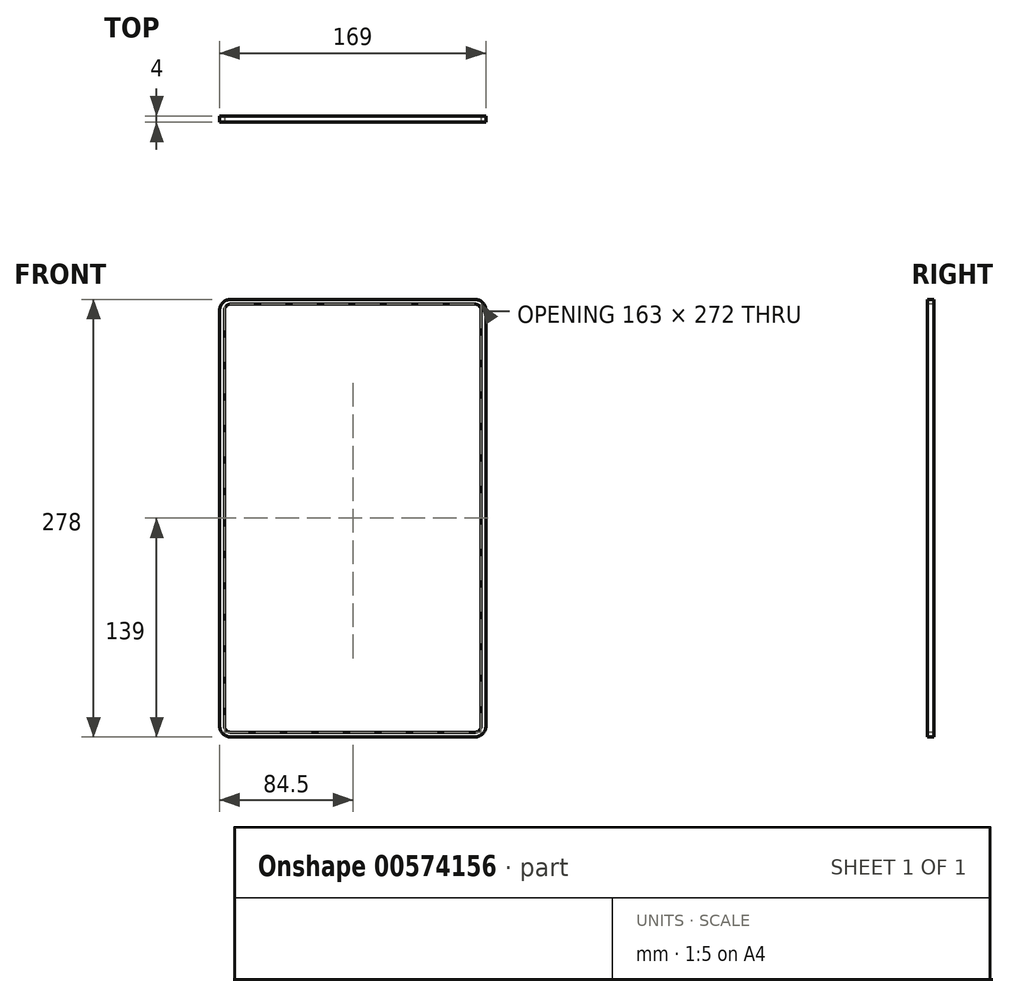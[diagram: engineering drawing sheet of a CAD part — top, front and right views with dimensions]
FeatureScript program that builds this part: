
annotation { "Feature Type Name" : "Feature", "Feature Type Description" : "" }
export const myFeature = defineFeature(function(context is Context, id is Id, definition is map)
    precondition{}
    {
        {
            var Q0;
            Q0=qCreatedBy(makeId("Front.planeOp"),FACE);
            var sketch = newSketch(context, id + "F0", { "sketchPlane" : qUnion([Q0])});
            skLineSegment(sketch, "E0.bottom", {"start": v(-77.5, 139) * mm, "end": v(77.5, 139) * mm});
            skLineSegment(sketch, "E0.top", {"start": v(-77.5, -139) * mm, "end": v(77.5, -139) * mm});
            skLineSegment(sketch, "E0.left", {"start": v(-84.5, 132) * mm, "end": v(-84.5, -132) * mm});
            skLineSegment(sketch, "E0.right", {"start": v(84.5, 132) * mm, "end": v(84.5, -132) * mm});
            skPoint(sketch, "E1.visualSharp", {"position": v(-84.5, 139) * mm});
            skArc(sketch, "E1.filletArc", {"start": v(-77.5, 139) * mm, "mid": v(-82.45, 136.95) * mm, "end": v(-84.5, 132) * mm});
            skPoint(sketch, "E2.visualSharp", {"position": v(84.5, 139) * mm});
            skArc(sketch, "E2.filletArc", {"start": v(84.5, 132) * mm, "mid": v(82.45, 136.95) * mm, "end": v(77.5, 139) * mm});
            skPoint(sketch, "E3.visualSharp", {"position": v(84.5, -139) * mm});
            skArc(sketch, "E3.filletArc", {"start": v(77.5, -139) * mm, "mid": v(82.45, -136.95) * mm, "end": v(84.5, -132) * mm});
            skPoint(sketch, "E4.visualSharp", {"position": v(-84.5, -139) * mm});
            skArc(sketch, "E4.filletArc", {"start": v(-84.5, -132) * mm, "mid": v(-82.45, -136.95) * mm, "end": v(-77.5, -139) * mm});
            skArc(sketch, "E5.0", {"start": v(-77.5, 136) * mm, "mid": v(-80.33, 134.83) * mm, "end": v(-81.5, 132) * mm});
            skLineSegment(sketch, "E5.1", {"start": v(-81.5, 132) * mm, "end": v(-81.5, -132) * mm});
            skLineSegment(sketch, "E5.2", {"start": v(-77.5, 136) * mm, "end": v(77.5, 136) * mm});
            skArc(sketch, "E5.3", {"start": v(-81.5, -132) * mm, "mid": v(-80.33, -134.83) * mm, "end": v(-77.5, -136) * mm});
            skArc(sketch, "E5.4", {"start": v(81.5, 132) * mm, "mid": v(80.33, 134.83) * mm, "end": v(77.5, 136) * mm});
            skLineSegment(sketch, "E5.5", {"start": v(81.5, 132) * mm, "end": v(81.5, -132) * mm});
            skArc(sketch, "E5.6", {"start": v(77.5, -136) * mm, "mid": v(80.33, -134.83) * mm, "end": v(81.5, -132) * mm});
            skLineSegment(sketch, "E5.7", {"start": v(-77.5, -136) * mm, "end": v(77.5, -136) * mm});
            skSolve(sketch);
        }
        {
            var Q0;
            Q0 = qSketchRegion(id + "F0", true);
            extrude(context, id + "F1", {"entities" : qUnion([Q0]), "oppositeDirection" : true, "depth" : 4 * mm, "offsetDistance" : 25 * mm});
        }
    });
